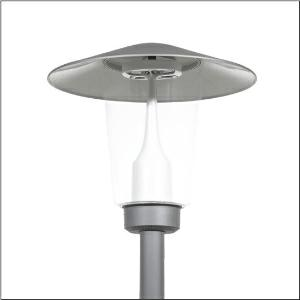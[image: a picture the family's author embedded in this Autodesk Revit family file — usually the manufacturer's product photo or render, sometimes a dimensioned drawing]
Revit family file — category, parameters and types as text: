
# Revit family: pilzleuchte_iq___st1_2a_5xa5235kf14hp_bd7e
name_source: partatom
category: Lighting Fixtures
units: mm (PartAtom-declared; Revit-internal decimal feet)

## family parameters
Cut with Voids When Loaded = No
Host = Face
Light Source = No
Part Type = Normal
Room Calculation Point = No
Round Connector Dimension = Use Diameter
Shared = No

## types (1)
- --- (1 x LED, 4990 lm, 33.6 W, 4000K)
    Apparent Load = 34 VA
    CIE Flux Codes = 23 60 92 98 100
    Color Rendering = 70
    Color Temperature = 4000K
    Default Elevation = 1800 mm
    Description = Mushroom Luminaire iQ, mast luminaire, Module 540 iQ-SR, primary light control with 3 zone facetted reflector, of plastic, silver coated, highly specular, structured, primary optical cover: cover, of PMMA, transparent, light distribution: ST1.2a, light emission: direct distribution, primary light characteristic: asymmetric, installation type: post-top, LED, High Power LED, rated luminous flux: 4.990lm, luminous efficacy: 149lm/W, light colour: 740, colour temperature: 4000K, control gear: ECG iQ, control: pre-setting: logarithmic dimming characteristic, Street-Remote, Auto-Match, Temp-Guard, Lumen-Switch, Night-Set, Smart-Wire, Light-Fading, Desk-Remote (wireless, voltage-free reading and setting of iQ features in the workshop via application-optimized NFC function/RFID function), optimised constant luminous flux control (CLO 2.0), with terminal, 6-pole, max. 2.5mm², mains connection: 230..240V, AC, 50/60Hz, start of lifetime: 34W, end of service life: 36W, reduction: 15W, luminaire housing, upper part, of glass-fibre reinforced polyester, coated, Siteco® metallic grey (DB 702S), diameter: 650mm, height: 586mm, spigot size: d x l = 76 x 70mm (post-top) | with reducer (optional accessory) 60 x 70mm, post-top mast mounting element, of diecast aluminium, coated, Siteco® metallic grey (DB 702S), Module 540 iQ-SR, traffic white (RAL 9016), equipment: Power, protection rating (complete): IP65, insulation class (complete): insulation class II (safety insulation), certification: CE, ENEC, VDE, packaging unit: 1 piece

Light Distribution: ST1.2a
    Height = 586 mm
    Lamp = 1 x LED
    Lamp Light Flux = 4990 lm
    Lamp Power = 33.6 W
    Lamp count = 1
    Length = 650 mm
    Luminous efficacy = 149 lm/W
    Manufacturer = Siteco
    ModVariant = No
    Model = 5XA5235KF14HP
    Number of Poles = 1
    OnlyDefault = Yes
    Power Factor = 1
    Product Name = Pilzleuchte iQ | ST1.2a
    Product group = mast luminaire | pylon top
    ProductGroupID = 6100
    Protection Class = Protection class II
    Protection Degree = IP 65
    RLX_Detail_Level = 1
    RLX_Emergency_Light_Flux = 0 lm
    RLX_Emergency_Type = 0
    RLX_Emergency_Type_DB = No
    RlxData = <blob elided: 51769 chars, md5=dba0e862>
    Socket = socket
    Standby Power = 0 W
    System Light Flux = 4990 lm
    System Power = 34 W
    Type Comments = factory setting: luminous flux: 100 % | dim-lin: 254 | 695 mA
    Type Image = l_1006077.jpg
    URL = http://relux.com
    VarID = @adj_166267
    Voltage = 0 V
    Weight = 0.00 kg
    Width = 0 mm  [stored 0 ft]

note: [stored X ft] marks values corroborated as IEEE doubles in the binary element streams (Revit-internal decimal feet)

## geometry (parser evidence)
native form markers: Blend x4, Sweep x10
no freeform markers — native parametric forms only
